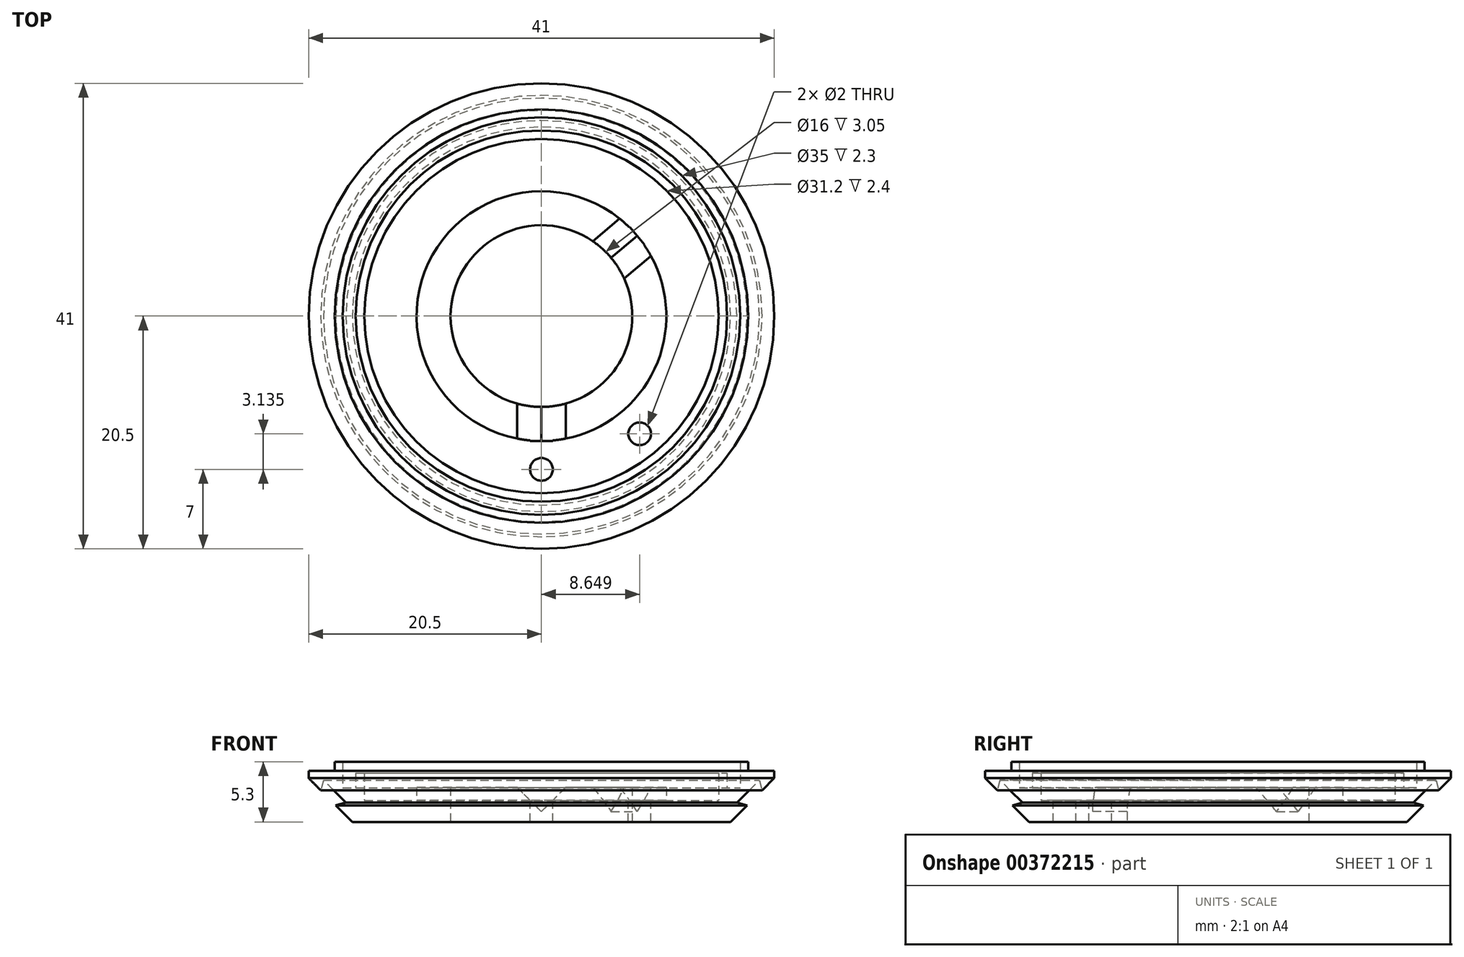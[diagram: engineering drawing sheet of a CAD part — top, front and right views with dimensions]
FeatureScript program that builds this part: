
annotation { "Feature Type Name" : "Feature", "Feature Type Description" : "" }
export const myFeature = defineFeature(function(context is Context, id is Id, definition is map)
    precondition{}
    {
        {
            var Q0;
            Q0=qCreatedBy(makeId("Front.planeOp"),FACE);
            var sketch = newSketch(context, id + "F0", { "sketchPlane" : qUnion([Q0])});
            skLineSegment(sketch, "E0", {"start": v(8, 0) * mm, "end": v(8, 3.05) * mm});
            skLineSegment(sketch, "E1", {"start": v(8, 3.05) * mm, "end": v(11, 3.05) * mm});
            skLineSegment(sketch, "E2", {"start": v(11, 3.05) * mm, "end": v(11, 1.9) * mm});
            skLineSegment(sketch, "E3", {"start": v(11, 1.9) * mm, "end": v(15.6, 1.9) * mm});
            skLineSegment(sketch, "E4", {"start": v(15.6, 1.9) * mm, "end": v(15.6, 4.3) * mm});
            skLineSegment(sketch, "E5", {"start": v(15.6, 4.3) * mm, "end": v(16.35, 4.3) * mm});
            skLineSegment(sketch, "E6", {"start": v(16.35, 4.3) * mm, "end": v(16.35, 3) * mm});
            skLineSegment(sketch, "E7", {"start": v(16.35, 3) * mm, "end": v(17.5, 3) * mm});
            skLineSegment(sketch, "E8", {"start": v(17.5, 3) * mm, "end": v(17.5, 5.3) * mm});
            skLineSegment(sketch, "E9", {"start": v(17.5, 5.3) * mm, "end": v(18.2, 5.3) * mm});
            skLineSegment(sketch, "E10", {"start": v(18.2, 5.3) * mm, "end": v(18.2, 4.5) * mm});
            skLineSegment(sketch, "E11", {"start": v(18.2, 4.5) * mm, "end": v(20.5, 4.5) * mm});
            skLineSegment(sketch, "E12", {"start": v(20.5, 4.5) * mm, "end": v(20.5, 3.85) * mm});
            skLineSegment(sketch, "E13", {"start": v(20.5, 3.85) * mm, "end": v(19.43, 2.78) * mm});
            skLineSegment(sketch, "E14", {"start": v(19.43, 2.78) * mm, "end": v(19.2, 3.68) * mm});
            skLineSegment(sketch, "E15", {"start": v(19.2, 3.68) * mm, "end": v(17.22, 1.7) * mm});
            skLineSegment(sketch, "E16", {"start": v(17.22, 1.7) * mm, "end": v(18.1, 1.46) * mm});
            skLineSegment(sketch, "E17", {"start": v(18.1, 1.46) * mm, "end": v(16.65, 0) * mm});
            skLineSegment(sketch, "E18", {"start": v(16.65, 0) * mm, "end": v(8, 0) * mm});
            skLineSegment(sketch, "E19", {"start": v(19.43, 2.78) * mm, "end": v(18.1, 1.46) * mm, "construction": true});
            skPoint(sketch, "E20", {"position": v(18.77, 2.12) * mm});
            skPoint(sketch, "E21", {"position": v(18.2, 2.69) * mm});
            skLineSegment(sketch, "E22", {"start": v(18.2, 2.69) * mm, "end": v(18.77, 2.12) * mm, "construction": true});
            skLineSegment(sketch, "E23", {"start": v(0, 0) * mm, "end": v(0, 5.3) * mm, "construction": true});
            skSolve(sketch);
        }
        {
            var Q0;
            Q0=makeQuery(id+"F0.imprint","IMPRINT",FACE,{"disambiguationData":[TD([[makeQuery(id+"F0.imprint","IMPRINT",EDGE,{"derivedFrom":sQuery(id+"F0.wireOp",EDGE,"E0")}),-1.0]])]});
            var Q1;
            Q1=sQuery(id+"F0.wireOp",EDGE,"E23");
            revolve(context, id + "F1", {"entities" : qUnion([Q0]), "axis" : qUnion([Q1]), "revolveType" : RevolveType.FULL});
        }
        {
            var Q0;
            Q0=qCreatedBy(makeId("Front.planeOp"),FACE);
            var sketch = newSketch(context, id + "F2", { "sketchPlane" : qUnion([Q0])});
            skLineSegment(sketch, "E24", {"start": v(0, 0) * mm, "end": v(0, 3.05) * mm, "construction": true});
            skLineSegment(sketch, "E25", {"start": v(0, 0.9) * mm, "end": v(2.15, 3.05) * mm});
            skLineSegment(sketch, "E26", {"start": v(0, 0.9) * mm, "end": v(-2.15, 3.05) * mm});
            skLineSegment(sketch, "E27", {"start": v(-2.15, 3.05) * mm, "end": v(2.15, 3.05) * mm});
            skSolve(sketch);
        }
        {
            var Q0;
            Q0=makeQuery(id+"F1.opRevolve","SWEPT_FACE",FACE,{"disambiguationData":[OSD([sQuery(id+"F0.wireOp",EDGE,"E1")])]});
            var sketch = newSketch(context, id + "F3", { "sketchPlane" : qUnion([Q0])});
            skLineSegment(sketch, "E28", {"start": v(0, -11) * mm, "end": v(0, 0) * mm});
            skLineSegment(sketch, "E29", {"start": v(0, 0) * mm, "end": v(8.43, 7.07) * mm});
            skSolve(sketch);
        }
        {
            var Q0;
            Q0=makeQuery(id+"F2.imprint","IMPRINT",FACE,{"disambiguationData":[TD([[makeQuery(id+"F2.imprint","IMPRINT",EDGE,{"derivedFrom":sQuery(id+"F2.wireOp",EDGE,"E25")}),1.0]])]});
            var Q1;
            Q1=sQuery(id+"F3.wireOp",EDGE,"E28");
            sweep(context, id + "F4", {"profiles" : qUnion([Q0]), "path" : qUnion([Q1])});
        }
        {
            var Q0;
            Q0=makeQuery(id+"F4.opSweep","SWEPT_BODY",BODY,{"disambiguationData":[OSD([sQuery(id+"F2.wireOp",EDGE,"E25"),sQuery(id+"F2.wireOp",EDGE,"E26"),sQuery(id+"F2.wireOp",EDGE,"E27"),sQuery(id+"F3.wireOp",EDGE,"E28")])]});
            var Q1;
            Q1=sQuery(id+"F0.wireOp",EDGE,"E23");
            circularPattern(context, id + "F5", {"entities" : qUnion([Q0]), "axis" : qUnion([Q1]), "angle" : 130 * degree, "instanceCount" : 2, "computeTransformsWithoutBuiltin" : true});
        }
        {
            var Q0;
            Q0=makeQuery(id+"F4.opSweep","SWEPT_BODY",BODY,{"disambiguationData":[OSD([sQuery(id+"F2.wireOp",EDGE,"E25"),sQuery(id+"F2.wireOp",EDGE,"E26"),sQuery(id+"F2.wireOp",EDGE,"E27"),sQuery(id+"F3.wireOp",EDGE,"E28")])]});
            var Q1;
            Q1=makeQuery(id+"F5.opPattern","COPY",BODY,{"derivedFrom":makeQuery(id+"F4.opSweep","SWEPT_BODY",BODY,{"disambiguationData":[OSD([sQuery(id+"F2.wireOp",EDGE,"E25"),sQuery(id+"F2.wireOp",EDGE,"E26"),sQuery(id+"F2.wireOp",EDGE,"E27"),sQuery(id+"F3.wireOp",EDGE,"E28")])]}),"instanceName":"1"});
            var Q2;
            Q2=makeQuery(id+"F1.opRevolve","SWEPT_BODY",BODY,{"disambiguationData":[OSD([sQuery(id+"F0.wireOp",EDGE,"E0"),sQuery(id+"F0.wireOp",EDGE,"E1"),sQuery(id+"F0.wireOp",EDGE,"E2"),sQuery(id+"F0.wireOp",EDGE,"E3"),sQuery(id+"F0.wireOp",EDGE,"E4"),sQuery(id+"F0.wireOp",EDGE,"E5"),sQuery(id+"F0.wireOp",EDGE,"E6"),sQuery(id+"F0.wireOp",EDGE,"E7"),sQuery(id+"F0.wireOp",EDGE,"E8"),sQuery(id+"F0.wireOp",EDGE,"E9"),sQuery(id+"F0.wireOp",EDGE,"E10"),sQuery(id+"F0.wireOp",EDGE,"E11"),sQuery(id+"F0.wireOp",EDGE,"E12"),sQuery(id+"F0.wireOp",EDGE,"E13"),sQuery(id+"F0.wireOp",EDGE,"E14"),sQuery(id+"F0.wireOp",EDGE,"E15"),sQuery(id+"F0.wireOp",EDGE,"E16"),sQuery(id+"F0.wireOp",EDGE,"E17"),sQuery(id+"F0.wireOp",EDGE,"E18")])]});
            booleanBodies(context, id + "F6", {"operationType" : BooleanOperationType.SUBTRACTION, "tools" : qUnion([Q0, Q1]), "targets" : qUnion([Q2])});
        }
        {
            var Q0;
            Q0=makeQuery(id+"F1.opRevolve","SWEPT_FACE",FACE,{"disambiguationData":[OSD([sQuery(id+"F0.wireOp",EDGE,"E3")])]});
            var sketch = newSketch(context, id + "F7", { "sketchPlane" : qUnion([Q0])});
            skCircle(sketch, "E30", {"center": v(0, 0) * mm, "radius": 13.5 * mm, "construction": true});
            skCircle(sketch, "E31", {"center": v(0, -13.5) * mm, "radius": 9.2 * mm, "construction": true});
            skCircle(sketch, "E32", {"center": v(0, -13.5) * mm, "radius": 1 * mm});
            skCircle(sketch, "E33", {"center": v(8.65, -10.37) * mm, "radius": 1 * mm});
            skSolve(sketch);
        }
        {
            var Q0;
            {Q0=qUnion([makeQuery(id+"F7.imprint","IMPRINT",FACE,{"disambiguationData":[TD([[makeQuery(id+"F7.imprint","IMPRINT",EDGE,{"derivedFrom":sQuery(id+"F7.wireOp",EDGE,"E32")}),1.0]])]}),makeQuery(id+"F7.imprint","IMPRINT",FACE,{"disambiguationData":[TD([[makeQuery(id+"F7.imprint","IMPRINT",EDGE,{"derivedFrom":sQuery(id+"F7.wireOp",EDGE,"E33")}),1.0]])]})]);}
            extrude(context, id + "F8", {"entities" : qUnion([Q0]), "operationType" : NewBodyOperationType.REMOVE, "endBound" : BoundingType.THROUGH_ALL, "oppositeDirection" : true, "depth" : 25 * mm});
        }
    });
